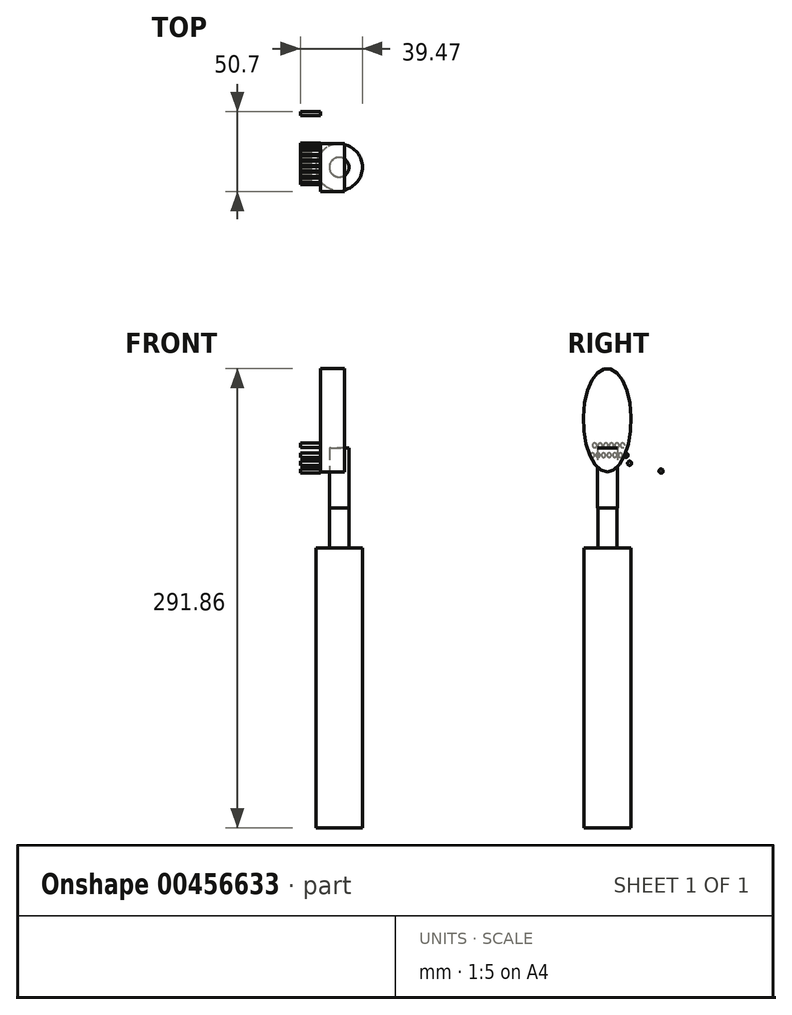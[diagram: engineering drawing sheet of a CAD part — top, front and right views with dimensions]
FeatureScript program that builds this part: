
annotation { "Feature Type Name" : "Feature", "Feature Type Description" : "" }
export const myFeature = defineFeature(function(context is Context, id is Id, definition is map)
    precondition{}
    {
        {
            var Q0;
            Q0=qCreatedBy(makeId("Right.planeOp"),FACE);
            var sketch = newSketch(context, id + "F0", { "sketchPlane" : qUnion([Q0])});
            skEllipse(sketch, "E0", {"center": v(-23.4, 55.77) * mm, "majorRadius": 32.89 * mm, "minorRadius": 15.17 * mm, "majorAxis": v(0, -1)});
            skSolve(sketch);
        }
        {
            var Q0;
            Q0 = qSketchRegion(id + "F0", true);
            extrude(context, id + "F1", {"entities" : qUnion([Q0]), "depth" : 15.24 * mm});
        }
        {
            var Q0;
            Q0=qCreatedBy(makeId("Top.planeOp"),FACE);
            var sketch = newSketch(context, id + "F2", { "sketchPlane" : qUnion([Q0])});
            skCircle(sketch, "E1", {"center": v(11.98, -23.23) * mm, "radius": 6.14 * mm});
            skSolve(sketch);
        }
        {
            var Q0;
            Q0 = qSketchRegion(id + "F2", true);
            extrude(context, id + "F3", {"entities" : qUnion([Q0]), "operationType" : NewBodyOperationType.ADD, "oppositeDirection" : true, "depth" : 203.2 * mm});
        }
        {
            var Q0;
            Q0=makeQuery(id+"F1.opExtrude","CAP_FACE",FACE,{"disambiguationData":[OSD([sQuery(id+"F0.wireOp",EDGE,"E0")])],"isStart":true});
            var sketch = newSketch(context, id + "F4", { "sketchPlane" : qUnion([Q0])});
            skCircle(sketch, "E2", {"center": v(13.6, 39.79) * mm, "radius": 1.43 * mm});
            skCircle(sketch, "E3.1.0.0", {"center": v(17.17, 39.79) * mm, "radius": 1.43 * mm});
            skCircle(sketch, "E3.2.0.0", {"center": v(20.72, 39.79) * mm, "radius": 1.43 * mm});
            skCircle(sketch, "E3.3.0.0", {"center": v(24.28, 39.79) * mm, "radius": 1.43 * mm});
            skCircle(sketch, "E3.4.0.0", {"center": v(27.83, 39.79) * mm, "radius": 1.43 * mm});
            skCircle(sketch, "E3.5.0.0", {"center": v(31.39, 39.79) * mm, "radius": 1.43 * mm});
            skLineSegment(sketch, "E3.direction1", {"start": v(13.6, 39.79) * mm, "end": v(17.17, 39.79) * mm, "construction": true});
            skCircle(sketch, "E4", {"center": v(11.48, 33.58) * mm, "radius": 1.33 * mm});
            skCircle(sketch, "E5.1.0.0", {"center": v(15.03, 33.58) * mm, "radius": 1.33 * mm});
            skCircle(sketch, "E5.2.0.0", {"center": v(18.59, 33.58) * mm, "radius": 1.33 * mm});
            skCircle(sketch, "E5.3.0.0", {"center": v(22.15, 33.58) * mm, "radius": 1.33 * mm});
            skCircle(sketch, "E5.4.0.0", {"center": v(25.7, 33.58) * mm, "radius": 1.33 * mm});
            skCircle(sketch, "E5.5.0.0", {"center": v(29.26, 33.58) * mm, "radius": 1.33 * mm});
            skCircle(sketch, "E5.6.0.0", {"center": v(32.81, 33.58) * mm, "radius": 1.33 * mm});
            skLineSegment(sketch, "E5.direction1", {"start": v(11.48, 33.58) * mm, "end": v(15.03, 33.58) * mm, "construction": true});
            skCircle(sketch, "E6", {"center": v(9.2, 28.47) * mm, "radius": 1.33 * mm});
            skCircle(sketch, "E7", {"center": v(-10.8, 23.5) * mm, "radius": 1.33 * mm});
            skSolve(sketch);
        }
        {
            var Q0;
            Q0 = qSketchRegion(id + "F4", true);
            extrude(context, id + "F5", {"entities" : qUnion([Q0]), "operationType" : NewBodyOperationType.ADD, "depth" : 12.7 * mm});
        }
        {
            var Q0;
            Q0=makeQuery(id+"F3.opExtrude","CAP_FACE",FACE,{"disambiguationData":[OSD([sQuery(id+"F2.wireOp",EDGE,"E1")])],"isStart":false});
            var sketch = newSketch(context, id + "F6", { "sketchPlane" : qUnion([Q0])});
            skCircle(sketch, "E8", {"center": v(11.98, 23.23) * mm, "radius": 14.79 * mm});
            skSolve(sketch);
        }
        {
            var Q0;
            Q0 = qSketchRegion(id + "F6", true);
            extrude(context, id + "F7", {"entities" : qUnion([Q0]), "operationType" : NewBodyOperationType.ADD, "oppositeDirection" : true, "depth" : 177.8 * mm});
        }
        {
            var Q0;
            Q0=makeQuery(id+"F3.opExtrude","CAP_FACE",FACE,{"disambiguationData":[OSD([sQuery(id+"F2.wireOp",EDGE,"E1")])],"isStart":true});
            var sketch = newSketch(context, id + "F8", { "sketchPlane" : qUnion([Q0])});
            skCircle(sketch, "E9", {"center": v(11.98, -23.23) * mm, "radius": 6.26 * mm});
            skSolve(sketch);
        }
        {
            var Q0;
            Q0 = qSketchRegion(id + "F8", true);
            extrude(context, id + "F9", {"entities" : qUnion([Q0]), "depth" : 38.1 * mm});
        }
    });
